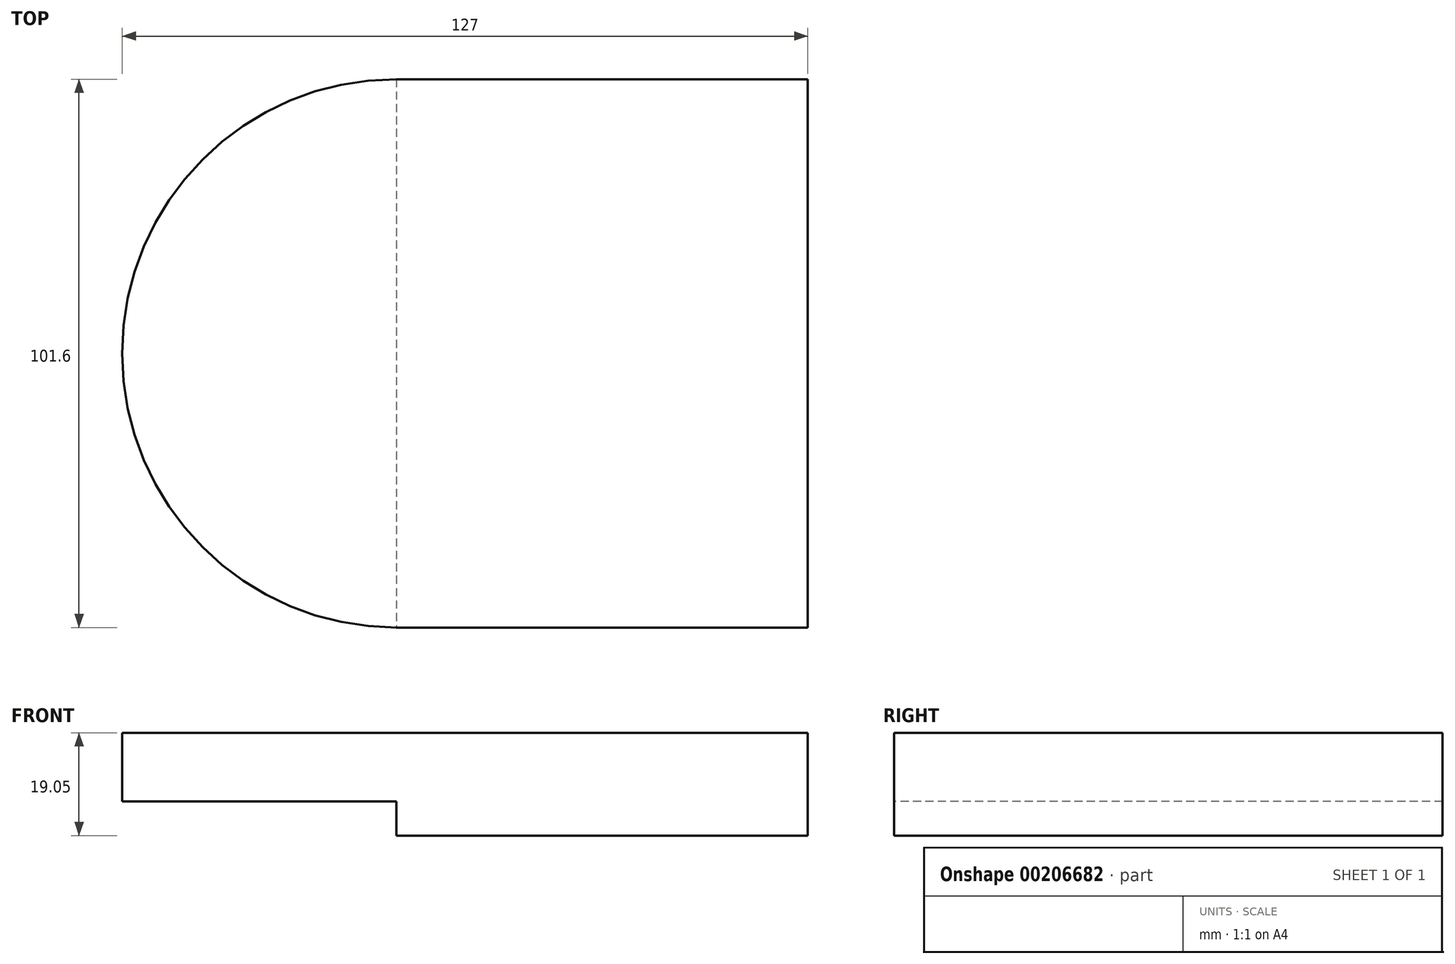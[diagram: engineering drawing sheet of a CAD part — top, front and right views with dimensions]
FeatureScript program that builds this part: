
annotation { "Feature Type Name" : "Feature", "Feature Type Description" : "" }
export const myFeature = defineFeature(function(context is Context, id is Id, definition is map)
    precondition{}
    {
        {
            var Q0;
            Q0=qCreatedBy(makeId("Top.planeOp"),FACE);
            var sketch = newSketch(context, id + "F0", { "sketchPlane" : qUnion([Q0])});
            skLineSegment(sketch, "E0.bottom", {"start": v(38.1, -50.8) * mm, "end": v(-38.1, -50.8) * mm});
            skLineSegment(sketch, "E0.top", {"start": v(38.1, 50.8) * mm, "end": v(-38.1, 50.8) * mm});
            skLineSegment(sketch, "E0.left", {"start": v(38.1, -50.8) * mm, "end": v(38.1, 50.8) * mm});
            skLineSegment(sketch, "E0.right", {"start": v(-38.1, -50.8) * mm, "end": v(-38.1, 50.8) * mm});
            skPoint(sketch, "E0.middle", {"position": v(0, 0) * mm});
            skArc(sketch, "E1", {"start": v(-38.1, 50.8) * mm, "mid": v(-88.9, 0) * mm, "end": v(-38.1, -50.8) * mm});
            skSolve(sketch);
        }
        {
            var Q0;
            Q0=makeQuery(id+"F0.imprint","IMPRINT",FACE,{"disambiguationData":[TD([[makeQuery(id+"F0.imprint","IMPRINT",EDGE,{"derivedFrom":sQuery(id+"F0.wireOp",EDGE,"E0.bottom")}),-1.0]])]});
            var Q1;
            Q1=makeQuery(id+"F0.imprint","IMPRINT",FACE,{"disambiguationData":[TD([[makeQuery(id+"F0.imprint","IMPRINT",EDGE,{"derivedFrom":sQuery(id+"F0.wireOp",EDGE,"E0.right")}),1.0]])]});
            extrude(context, id + "F1", {"entities" : qUnion([Q0, Q1]), "depth" : 19.05 * mm});
        }
        {
            var Q0;
            Q0=makeQuery(id+"F1.opExtrude","SWEPT_FACE",FACE,{"disambiguationData":[OSD([sQuery(id+"F0.wireOp",EDGE,"E0.bottom")])]});
            var sketch = newSketch(context, id + "F2", { "sketchPlane" : qUnion([Q0])});
            skLineSegment(sketch, "E2", {"start": v(38.1, 0) * mm, "end": v(38.1, -16.46) * mm});
            skLineSegment(sketch, "E3", {"start": v(38.1, -16.46) * mm, "end": v(25.4, -16.46) * mm});
            skLineSegment(sketch, "E4", {"start": v(25.4, -16.46) * mm, "end": v(25.4, 0) * mm});
            skLineSegment(sketch, "E5", {"start": v(25.4, 0) * mm, "end": v(25.4, 6.35) * mm});
            skLineSegment(sketch, "E6", {"start": v(25.4, 6.35) * mm, "end": v(-105.34, 6.35) * mm});
            skLineSegment(sketch, "E7", {"start": v(-105.34, 6.35) * mm, "end": v(-105.34, -26.1) * mm});
            skLineSegment(sketch, "E8.bottom", {"start": v(25.4, 6.35) * mm, "end": v(-98.24, 6.35) * mm});
            skLineSegment(sketch, "E8.top", {"start": v(25.4, -12.2) * mm, "end": v(-98.24, -12.2) * mm});
            skLineSegment(sketch, "E8.left", {"start": v(25.4, 6.35) * mm, "end": v(25.4, -12.2) * mm});
            skLineSegment(sketch, "E8.right", {"start": v(-98.24, 6.35) * mm, "end": v(-98.24, -12.2) * mm});
            skSolve(sketch);
        }
        {
            var Q0;
            {var subQ2=sQuery(id+"F2.wireOp",EDGE,"E8.top");Q0=makeQuery(id+"F2.imprint","IMPRINT",FACE,{"disambiguationData":[TD([[makeQuery(id+"F2.imprint","IMPRINT",EDGE,{"derivedFrom":subQ2}),-1.0]])]});}
            var Q1;
            {var subQ0=sQuery(id+"F2.wireOp",EDGE,"E8.left");var subQ1=sQuery(id+"F2.wireOp",EDGE,"E8.bottom");var subQ2=makeQuery(id+"F2.imprint","INTERSECT",VERTEX,{"derivedFrom":[subQ1,subQ0]});Q1=makeQuery(id+"F2.imprint","IMPRINT",FACE,{"disambiguationData":[TD([[makeQuery(id+"F2.imprint","IMPRINT",EDGE,{"disambiguationData":[TD([[subQ2,-1.0]])],"derivedFrom":subQ0}),-1.0]])]});}
            extrude(context, id + "F3", {"entities" : qUnion([Q0, Q1]), "operationType" : NewBodyOperationType.REMOVE, "oppositeDirection" : true, "depth" : 164.85 * mm});
        }
        {
            var Q0;
            Q0=makeQuery(id+"F1.opExtrude","SWEPT_FACE",FACE,{"disambiguationData":[OSD([sQuery(id+"F0.wireOp",EDGE,"E0.bottom")])]});
            cPlane(context, id + "F4", {"entities" : qUnion([Q0]), "cplaneType" : CPlaneType.OFFSET, "offset" : 12.7 * mm, "oppositeDirection" : true, "width" : 152.4 * mm, "height" : 152.4 * mm});
        }
        {
            var Q0;
            Q0=qCreatedBy(id+"F4.planeOp",FACE);
            var sketch = newSketch(context, id + "F5", { "sketchPlane" : qUnion([Q0])});
            skPoint(sketch, "E9.0", {"position": v(38.1, 19.05) * mm});
            skLineSegment(sketch, "E10", {"start": v(38.1, 19.05) * mm, "end": v(-40.5, 19.05) * mm});
            skLineSegment(sketch, "E11", {"start": v(38.1, 19.05) * mm, "end": v(-16.9, 50.8) * mm});
            skSolve(sketch);
        }
        {
            var Q0;
            Q0=sQuery(id+"F5.wireOp",VERTEX,"E11.end");
            var Q1;
            Q1=sQuery(id+"F5.wireOp",VERTEX,"E9.0");
            var Q2;
            Q2=makeQuery(id+"F1.opExtrude","CAP_VERTEX",VERTEX,{"disambiguationData":[OSD([sQuery(id+"F0.wireOp",EDGE,"E0.top"),sQuery(id+"F0.wireOp",EDGE,"E0.left")])],"isStart":false});
            cPlane(context, id + "F6", {"entities" : qUnion([Q0, Q1, Q2]), "cplaneType" : CPlaneType.THREE_POINT, "offset" : 25.4 * mm, "width" : 152.4 * mm, "height" : 152.4 * mm});
        }
    });
